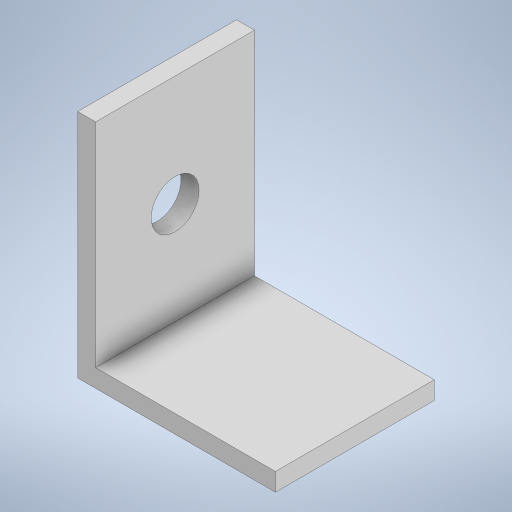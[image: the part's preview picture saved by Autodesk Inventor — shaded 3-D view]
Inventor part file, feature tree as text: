
AUTODESK INVENTOR PART (.ipt)
format: ipt  version: 2023 (Build 270158000, 158)  size: 226,304 bytes
history: native  units: mm
features: sketch x3, extrude x2, hole x1
ambient origin geometry x8: Origin, YZ Plane, XZ Plane, XY Plane, X Axis, Y Axis, Z Axis, Center Point
bodies: Volumenkörper1 (feature_tree)
feature tree (6):
  extrude  "Extrusion1"  Depth=26.5mm
  extrude  "Extrusion2"  Depth=35.5mm
  hole  "Bohrung1"  [1 undecoded]
  sketch  "Skizze1"  dims[d0=38.5mm d1=26.5mm]
  sketch  "Skizze2"  dims[d2=33.0mm d3=0.0mm d4=35.5mm]
  sketch  "Skizze3"  dims[d5=0.0mm d6=0.0mm d7=8.0mm d8=6.0mm d9=4.0mm d10=2.0mm d11=90.0deg d12=8.0mm d13=20.594885mm d14=0.0mm d15=17.0mm]
note: 1 required parameter value undecoded (feature->parameter linkage not recoverable at this tier; creation-order binding heuristic only, values carry confidence <= 0.55)
